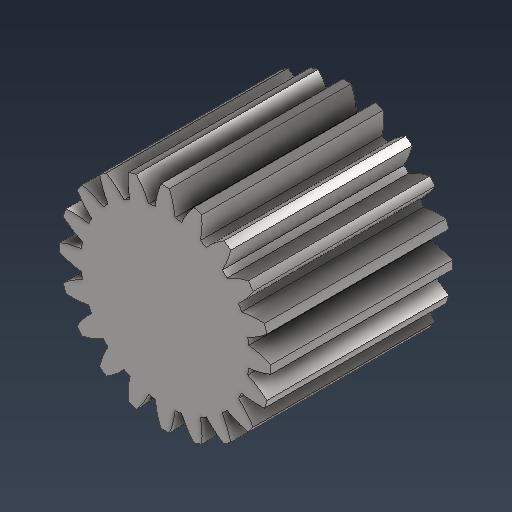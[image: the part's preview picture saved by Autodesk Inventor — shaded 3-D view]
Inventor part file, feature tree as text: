
AUTODESK INVENTOR PART (.ipt)
format: ipt  version: 2021 (Build 250183000, 183)  size: 296,960 bytes
history: native  units: mm (DEFAULTED — no unit token found)
features: plane x3, other x3, sketch x2, extrude x1
ambient origin geometry x8: Origin, YZ Plane, XZ Plane, XY Plane, X Axis, Y Axis, Z Axis, Center Point
bodies: Solid1 (feature_tree)
feature tree (9):
  extrude  "Extrusion1"  Depth=1.7mm TaperAngle=0.0deg
  plane  "Work Plane2"
  plane  "Work Plane8"
  plane  "Work Plane9"
  other  "Engrenagem reta"
  sketch  "Sketch1"  dims[d0=1.979988mm d1=1.7mm d2=0.0mm]
  sketch  "Sketch2"  dims[d3=1.8mm d4=10.0mm d5=0.0mm d16=3.597588mm d17=0.0mm d34=1.570796mm d39=0.0mm d41=0.0mm d43=3.597588mm d46=3.597588mm d47=0.0mm d48=0.0mm]
  other  "Srf1"
  other  "Diâmetro do flanco"
